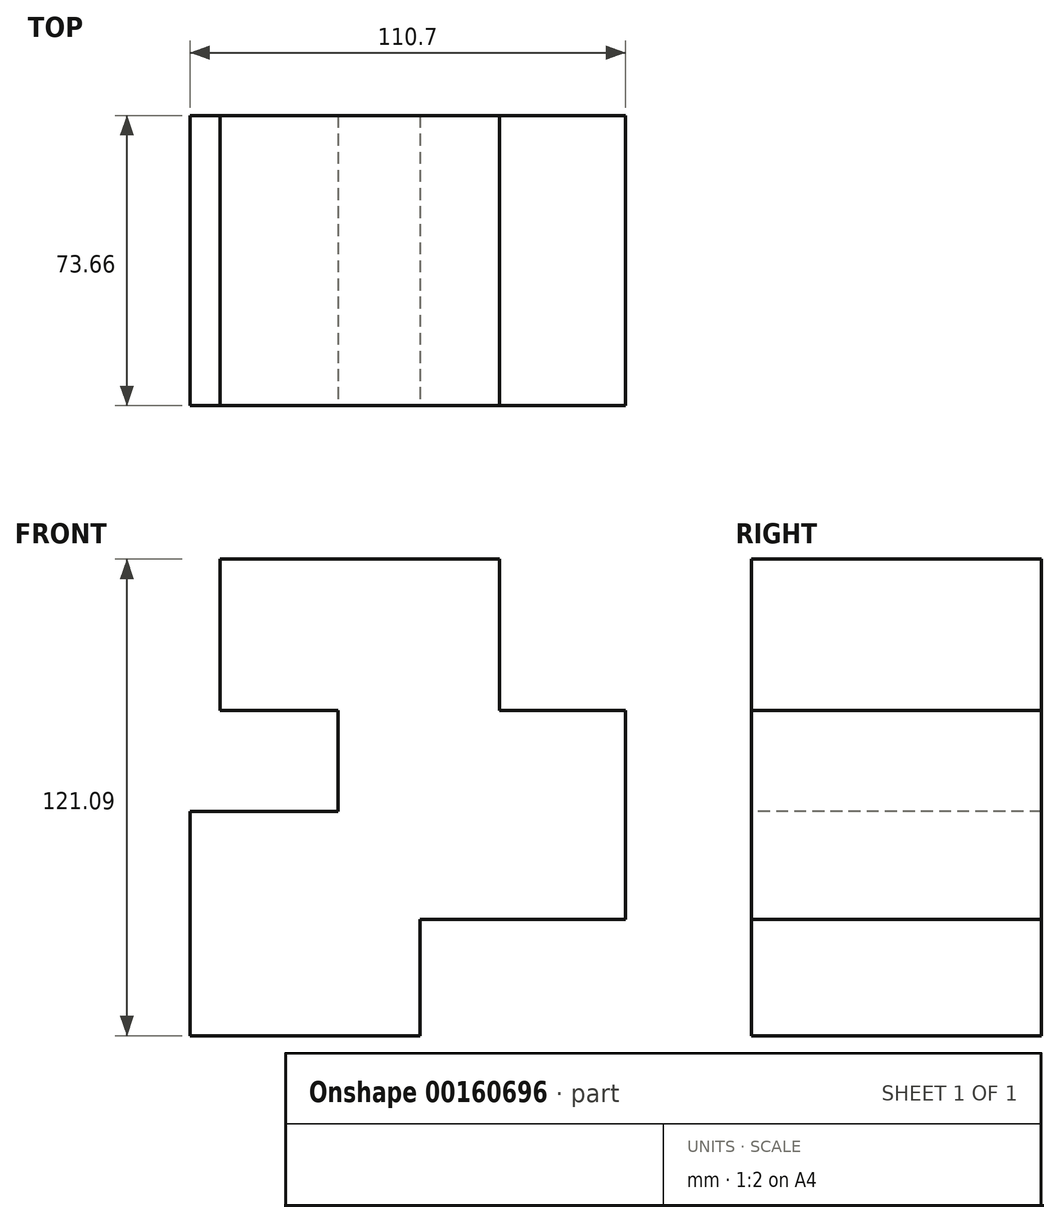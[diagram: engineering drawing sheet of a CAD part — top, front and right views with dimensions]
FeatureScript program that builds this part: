
annotation { "Feature Type Name" : "Feature", "Feature Type Description" : "" }
export const myFeature = defineFeature(function(context is Context, id is Id, definition is map)
    precondition{}
    {
        {
            var Q0;
            Q0=qCreatedBy(makeId("Front.planeOp"),FACE);
            var sketch = newSketch(context, id + "F0", { "sketchPlane" : qUnion([Q0])});
            skLineSegment(sketch, "E0", {"start": v(-32.8, 8.86) * mm, "end": v(-32.8, 47.35) * mm});
            skLineSegment(sketch, "E1", {"start": v(-32.8, 47.35) * mm, "end": v(38.1, 47.35) * mm});
            skLineSegment(sketch, "E2", {"start": v(38.1, 47.35) * mm, "end": v(38.1, 8.86) * mm});
            skLineSegment(sketch, "E3", {"start": v(38.1, 8.86) * mm, "end": v(70.2, 8.86) * mm});
            skLineSegment(sketch, "E4", {"start": v(70.2, 8.86) * mm, "end": v(70.2, -44.2) * mm});
            skLineSegment(sketch, "E5", {"start": v(70.2, -44.2) * mm, "end": v(17.9, -44.2) * mm});
            skLineSegment(sketch, "E6", {"start": v(17.9, -44.2) * mm, "end": v(17.9, -73.74) * mm});
            skLineSegment(sketch, "E7", {"start": v(17.9, -73.74) * mm, "end": v(-40.5, -73.74) * mm});
            skLineSegment(sketch, "E8", {"start": v(-40.5, -73.74) * mm, "end": v(-40.5, -16.8) * mm});
            skLineSegment(sketch, "E9", {"start": v(-40.5, -16.8) * mm, "end": v(-2.9, -16.8) * mm});
            skLineSegment(sketch, "E10", {"start": v(-2.9, -16.8) * mm, "end": v(-2.9, 8.86) * mm});
            skLineSegment(sketch, "E11", {"start": v(-2.9, 8.86) * mm, "end": v(-32.8, 8.86) * mm});
            skSolve(sketch);
        }
        {
            var Q0;
            Q0=makeQuery(id+"F0.imprint","IMPRINT",FACE,{"disambiguationData":[TD([[makeQuery(id+"F0.imprint","IMPRINT",EDGE,{"derivedFrom":sQuery(id+"F0.wireOp",EDGE,"E0")}),-1.0]])]});
            extrude(context, id + "F1", {"entities" : qUnion([Q0]), "oppositeDirection" : true, "depth" : 73.66 * mm});
        }
    });
